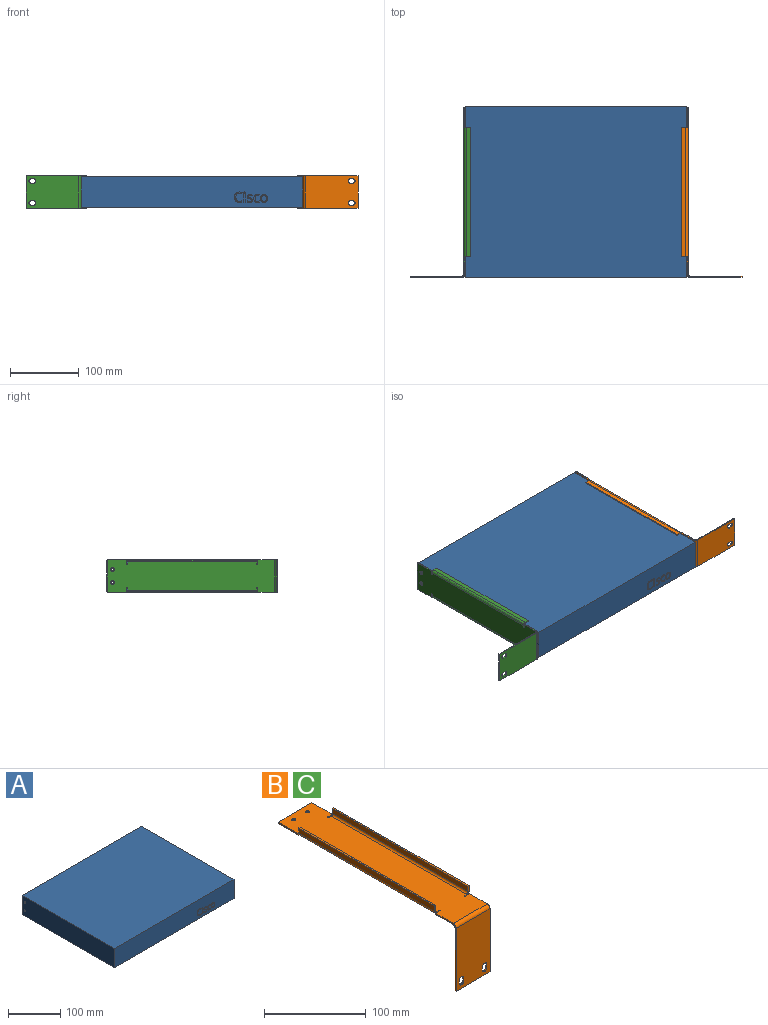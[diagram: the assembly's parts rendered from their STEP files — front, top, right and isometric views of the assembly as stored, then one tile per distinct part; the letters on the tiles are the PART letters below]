
ASSEMBLY  parts=3 mates=4
PART A: 99 faces, bbox 323x248.5x44.5 mm
  f0: plane 323x44.5mm, normal (0,-1,0), area 14138.3mm2, adj f2,f3,f4,f5,f15,f16,f17,f18
  f1: plane 323x44.5mm, normal (0,1,0), area 14373.5mm2, adj f2,f3,f4,f5
  f2: plane 248.5x44.5mm, normal (-1,0,0), area 11033.1mm2, adj f0,f1,f4,f5,f6,f7
  f3: plane 248.5x44.5mm, normal (1,0,0), area 11033.1mm2, adj f0,f1,f4,f5,f6,f7
  f4: plane 323x248.5mm, normal (0,0,1), area 80265.5mm2, adj f0,f1,f2,f3
  f5: plane 323x248.5mm, normal (0,0,-1), area 80265.5mm2, adj f0,f1,f2,f3
  f6: cylinder r=2mm len=323mm, axis (1,0,0), area 4058.9mm2, adj f2,f3
  f7: cylinder r=2mm len=323mm, axis (1,0,0), area 4058.9mm2, adj f2,f3
  f8: extruded ~5x3.23mm, area 17mm2, adj f9,f24,f25,f98
  f9: extruded ~5x3.22mm, area 16.9mm2, adj f8,f10,f25,f98
  f10: extruded ~5x2.48mm, area 14.1mm2, adj f9,f11,f25,f98
  f11: extruded ~5x2.52mm, area 14.3mm2, adj f10,f12,f25,f98
  f12: extruded ~5x3.21mm, area 16.9mm2, adj f11,f13,f25,f98
  f13: extruded ~5x3.24mm, area 17mm2, adj f12,f14,f25,f98
  f14: extruded ~5x2.5mm, area 14.2mm2, adj f13,f24,f25,f98
  f15: extruded ~5x4.23mm, area 22.7mm2, adj f0,f16,f23,f25
  f16: extruded ~5x4.18mm, area 22.5mm2, adj f0,f15,f17,f25
  f17: extruded ~5x3.69mm, area 20.7mm2, adj f0,f16,f18,f25
  f18: extruded ~5x3.76mm, area 20.9mm2, adj f0,f17,f19,f25
  f19: extruded ~5x4.22mm, area 22.7mm2, adj f0,f18,f20,f25
  f20: extruded ~5x3.05mm, area 15.7mm2, adj f0,f19,f21,f25
  f21: extruded ~5x2mm, area 13.6mm2, adj f0,f20,f22,f25
  f22: extruded ~5x2.64mm, area 13.8mm2, adj f0,f21,f23,f25
  f23: extruded ~5x3.77mm, area 21mm2, adj f0,f15,f22,f25
  f24: extruded ~5x2.49mm, area 14.2mm2, adj f8,f14,f25,f98
  f25: plane 11.48x10.17mm, normal (0,-1,0), area 47.1mm2, adj f8,f9,f10,f11,f12,f13,f14,f15
  f26: extruded ~5x3.72mm, area 20.7mm2, adj f0,f27,f40,f41
  f27: extruded ~5x2.8mm, area 14.4mm2, adj f0,f26,f28,f41
  f28: plane 5x1.48mm, normal (-1,0,0), area 7.4mm2, adj f0,f27,f29,f41
  f29: extruded ~5x2.84mm, area 14.6mm2, adj f0,f28,f30,f41
  f30: extruded ~5x2.44mm, area 13.9mm2, adj f0,f29,f31,f41
  f31: extruded ~5x3.13mm, area 16.5mm2, adj f0,f30,f32,f41
  f32: extruded ~5x4.3mm, area 31.2mm2, adj f0,f31,f33,f41
  f33: extruded ~5x1.16mm, area 5.9mm2, adj f0,f32,f34,f41
  f34: extruded ~5x1.21mm, area 6.3mm2, adj f0,f33,f35,f41
  f35: plane 5x1.42mm, normal (-0.94,0,0.34), area 7.6mm2, adj f0,f34,f36,f41
  f36: extruded ~5x1.25mm, area 6.6mm2, adj f0,f35,f37,f41
  f37: extruded ~5x1.6mm, area 8mm2, adj f0,f36,f38,f41
  f38: extruded ~5x3.81mm, area 21.2mm2, adj f0,f37,f39,f41
  f39: extruded ~5x4.29mm, area 23mm2, adj f0,f38,f40,f41
  f40: extruded ~5x4.19mm, area 22.5mm2, adj f0,f26,f39,f41
  f41: plane 11.48x8mm, normal (0,-1,0), area 32.5mm2, adj f26,f27,f28,f29,f30,f31,f32,f33
  f42: extruded ~5x2.38mm, area 13.8mm2, adj f0,f43,f66,f67
  f43: extruded ~5x1.83mm, area 10mm2, adj f0,f42,f44,f67
  f44: extruded ~5x2.66mm, area 15.3mm2, adj f0,f43,f45,f67
  f45: extruded ~5x1.94mm, area 10.5mm2, adj f0,f44,f46,f67
  f46: extruded ~5x0.73mm, area 4.8mm2, adj f0,f45,f47,f67
  f47: extruded ~5x0.76mm, area 4mm2, adj f0,f46,f48,f67
  f48: extruded ~5x1.03mm, area 6.3mm2, adj f0,f47,f49,f67
  f49: extruded ~5x1.8mm, area 9.3mm2, adj f0,f48,f50,f67
  f50: extruded ~5x3.02mm, area 15.6mm2, adj f0,f49,f51,f67
  f51: plane 5x1.36mm, normal (-0.92,0,0.4), area 7.4mm2, adj f0,f50,f52,f67
  f52: extruded ~5x3.5mm, area 18mm2, adj f0,f51,f53,f67
  f53: extruded ~5x3.02mm, area 15.8mm2, adj f0,f52,f54,f67
  f54: extruded ~5x2.14mm, area 12.5mm2, adj f0,f53,f55,f67
  f55: extruded ~5x1.3mm, area 6.8mm2, adj f0,f54,f56,f67
  f56: extruded ~5x0.97mm, area 6.9mm2, adj f0,f55,f57,f67
  f57: extruded ~5x2.2mm, area 12.1mm2, adj f0,f56,f58,f67
  f58: extruded ~5x2.19mm, area 12.3mm2, adj f0,f57,f59,f67
  f59: extruded ~5x1.11mm, area 6.4mm2, adj f0,f58,f60,f67
  f60: extruded ~5x1.28mm, area 7.7mm2, adj f0,f59,f61,f67
  f61: extruded ~5x2.02mm, area 10.4mm2, adj f0,f60,f62,f67
  f62: extruded ~5x1.76mm, area 8.9mm2, adj f0,f61,f63,f67
  f63: extruded ~5x1.71mm, area 9.1mm2, adj f0,f62,f64,f67
  f64: plane 5x1.56mm, normal (1,0,0), area 7.8mm2, adj f0,f63,f65,f67
  f65: extruded ~5x3.43mm, area 17.7mm2, adj f0,f64,f66,f67
  f66: extruded ~5x3.23mm, area 17mm2, adj f0,f42,f65,f67
  f67: plane 11.48x7.85mm, normal (0,-1,0), area 37.6mm2, adj f42,f43,f44,f45,f46,f47,f48,f49
  f68: extruded ~5x0.84mm, area 4.6mm2, adj f0,f69,f75,f76
  f69: extruded ~5x0.84mm, area 4.6mm2, adj f0,f68,f70,f76
  f70: extruded ~5x0.71mm, area 3.9mm2, adj f0,f69,f71,f76
  f71: extruded ~5x0.7mm, area 3.8mm2, adj f0,f70,f72,f76
  f72: extruded ~5x0.84mm, area 4.6mm2, adj f0,f71,f73,f76
  f73: extruded ~5x0.84mm, area 4.6mm2, adj f0,f72,f74,f76
  f74: extruded ~5x0.7mm, area 3.8mm2, adj f0,f73,f75,f76
  f75: extruded ~5x0.71mm, area 3.9mm2, adj f0,f68,f74,f76
  f76: plane 2.23x1.98mm, normal (0,-1,0), area 3.6mm2, adj f68,f69,f70,f71,f72,f73,f74,f75
  f77: plane 5x1.68mm, normal (0,0,1), area 8.4mm2, adj f0,f78,f80,f81
  f78: plane 11.07x5mm, normal (-1,0,0), area 55.4mm2, adj f0,f77,f79,f81
  f79: plane 5x1.68mm, normal (0,0,-1), area 8.4mm2, adj f0,f78,f80,f81
  f80: plane 11.07x5mm, normal (1,0,0), area 55.4mm2, adj f0,f77,f79,f81
  f81: plane 11.07x1.68mm, normal (0,-1,0), area 18.6mm2, adj f77,f78,f79,f80
  f82: extruded ~5x3.84mm, area 21.6mm2, adj f0,f83,f96,f97
  f83: extruded ~5x3.36mm, area 17.4mm2, adj f0,f82,f84,f97
  f84: plane 5x1.47mm, normal (-0.9,0,0.44), area 8.2mm2, adj f0,f83,f85,f97
  f85: extruded ~5x4.06mm, area 20.9mm2, adj f0,f84,f86,f97
  f86: extruded ~5x3.79mm, area 19.8mm2, adj f0,f85,f87,f97
  f87: extruded ~5x2.65mm, area 18.4mm2, adj f0,f86,f88,f97
  f88: extruded ~5x4mm, area 20.6mm2, adj f0,f87,f89,f97
  f89: extruded ~5.63x5mm, area 30.2mm2, adj f0,f88,f90,f97
  f90: extruded ~5.04x5mm, area 27.9mm2, adj f0,f89,f91,f97
  f91: extruded ~5x3.79mm, area 19.3mm2, adj f0,f90,f92,f97
  f92: plane 5x1.5mm, normal (-1,0,0), area 7.5mm2, adj f0,f91,f93,f97
  f93: extruded ~5x3.53mm, area 17.9mm2, adj f0,f92,f94,f97
  f94: extruded ~5x3.87mm, area 21.6mm2, adj f0,f93,f95,f97
  f95: extruded ~5x4.48mm, area 23.9mm2, adj f0,f94,f96,f97
  f96: extruded ~5x4.44mm, area 23.8mm2, adj f0,f82,f95,f97
  f97: plane 15.18x11.17mm, normal (0,-1,0), area 47.7mm2, adj f82,f83,f84,f85,f86,f87,f88,f89
  f98: plane 8.65x6.7mm, normal (0,-1,0), area 48.1mm2, adj f8,f9,f10,f11,f12,f13,f14,f24
PART B: 58 faces, bbox 48.7x248x88.4 mm
  f0: plane 3.5x1.6mm, normal (-1,0,0), area 5.6mm2, adj f1,f10,f11,f12
  f1: cylinder r=3.25mm len=6.5mm, axis (0,1,0), area 16.3mm2, adj f0,f2,f11,f12
  f2: plane 3.5x1.6mm, normal (1,0,0), area 5.6mm2, adj f1,f10,f11,f12
  f3: plane 3.5x1.6mm, normal (-1,0,0), area 5.6mm2, adj f4,f9,f11,f12
  f4: cylinder r=3.25mm len=6.5mm, axis (0,1,0), area 16.3mm2, adj f3,f5,f11,f12
  f5: plane 3.5x1.6mm, normal (1,0,0), area 5.6mm2, adj f4,f9,f11,f12
  f6: plane 76.1x1.6mm, normal (-1,0,0), area 121.8mm2, adj f8,f11,f12,f53
  f7: plane 76.1x1.6mm, normal (1,0,0), area 121.8mm2, adj f8,f11,f12,f52
  f8: plane 47.1x1.6mm, normal (0,0,-1), area 75.4mm2, adj f6,f7,f11,f12
  f9: cylinder r=3.25mm len=6.5mm, axis (0,1,0), area 16.3mm2, adj f3,f5,f11,f12
  f10: cylinder r=3.25mm len=6.5mm, axis (0,1,0), area 16.3mm2, adj f0,f2,f11,f12
  f11: plane 76.1x47.1mm, normal (0,1,0), area 3472.4mm2, adj f0,f1,f2,f3,f4,f5,f6,f7
  f12: plane 76.1x47.1mm, normal (0,-1,0), area 3472.4mm2, adj f0,f1,f2,f3,f4,f5,f6,f7
  f13: plane 24.4x1.6mm, normal (-1,0,0), area 39mm2, adj f15,f16,f24,f53
  f14: plane 28.3x1.6mm, normal (1,0,0), area 45.3mm2, adj f15,f16,f18,f30
  f15: plane 244.1x47.1mm, normal (0,0,-1), area 10231.7mm2, adj f13,f14,f17,f18,f19,f22,f23,f24
  f16: plane 244.1x47.1mm, normal (0,0,1), area 10263.1mm2, adj f13,f14,f17,f18,f19,f20,f21,f22
  f17: plane 28.3x1.6mm, normal (-1,0,0), area 45.3mm2, adj f15,f16,f18,f27
  f18: plane 47.1x1.6mm, normal (0,1,0), area 75.4mm2, adj f14,f15,f16,f17
  f19: plane 24.4x1.6mm, normal (1,0,0), area 39mm2, adj f15,f16,f33,f52
  f20: cylinder r=2mm len=4mm, axis (0,0,-1), area 7.5mm2, adj f16,f56
  f21: cylinder r=2mm len=4mm, axis (0,0,-1), area 7.5mm2, adj f16,f57
  f22: cylinder r=0.85mm len=1.7mm, axis (0,0,1), area 4.3mm2, adj f15,f16,f23,f24
  f23: plane 2.6x1.6mm, normal (0,-1,0), area 4.2mm2, adj f15,f16,f22,f40
  f24: plane 5.7x1.6mm, normal (0,1,0), area 9.1mm2, adj f13,f15,f16,f22
  f25: cylinder r=0.85mm len=1.7mm, axis (0,0,1), area 4.3mm2, adj f15,f16,f26,f27
  f26: plane 2.6x1.6mm, normal (0,1,0), area 4.2mm2, adj f15,f16,f25,f39
  f27: plane 5.7x1.6mm, normal (0,-1,0), area 9.1mm2, adj f15,f16,f17,f25
  f28: cylinder r=0.85mm len=1.7mm, axis (0,0,1), area 4.3mm2, adj f15,f16,f29,f30
  f29: plane 2.6x1.6mm, normal (0,1,0), area 4.2mm2, adj f15,f16,f28,f49
  f30: plane 5.7x1.6mm, normal (0,-1,0), area 9.1mm2, adj f14,f15,f16,f28
  f31: cylinder r=0.85mm len=1.7mm, axis (0,0,1), area 4.3mm2, adj f15,f16,f32,f33
  f32: plane 2.6x1.6mm, normal (0,-1,0), area 4.2mm2, adj f15,f16,f31,f48
  f33: plane 5.7x1.6mm, normal (0,1,0), area 9.1mm2, adj f15,f16,f19,f31
  f34: plane 6.1x1.6mm, normal (0,1,0), area 9.8mm2, adj f36,f37,f38,f39
  f35: plane 6.1x1.6mm, normal (0,-1,0), area 9.8mm2, adj f36,f37,f38,f40
  f36: plane 188x1.6mm, normal (0,0,1), area 300.8mm2, adj f34,f35,f37,f38
  f37: plane 188x6.1mm, normal (-1,0,0), area 1146.8mm2, adj f34,f35,f36,f41
  f38: plane 188x6.1mm, normal (1,0,0), area 1146.8mm2, adj f34,f35,f36,f42
  f39: plane 3.9x3.9mm, normal (0,1,0), area 7.8mm2, adj f26,f34,f41,f42
  f40: plane 3.9x3.9mm, normal (0,-1,0), area 7.8mm2, adj f23,f35,f41,f42
  f41: cylinder r=3.9mm len=188mm, axis (0,1,0), area 1151.7mm2, adj f15,f37,f39,f40
  f42: cylinder r=2.3mm len=188mm, axis (0,1,0), area 679.2mm2, adj f16,f38,f39,f40
  f43: plane 6.1x1.6mm, normal (0,-1,0), area 9.8mm2, adj f45,f46,f47,f48
  f44: plane 6.1x1.6mm, normal (0,1,0), area 9.8mm2, adj f45,f46,f47,f49
  f45: plane 188x1.6mm, normal (0,0,1), area 300.8mm2, adj f43,f44,f46,f47
  f46: plane 188x6.1mm, normal (1,0,0), area 1146.8mm2, adj f43,f44,f45,f50
  f47: plane 188x6.1mm, normal (-1,0,0), area 1146.8mm2, adj f43,f44,f45,f51
  f48: plane 3.9x3.9mm, normal (0,-1,0), area 7.8mm2, adj f32,f43,f50,f51
  f49: plane 3.9x3.9mm, normal (0,1,0), area 7.8mm2, adj f29,f44,f50,f51
  f50: cylinder r=3.9mm len=188mm, axis (0,-1,0), area 1151.7mm2, adj f15,f46,f48,f49
  f51: cylinder r=2.3mm len=188mm, axis (0,-1,0), area 679.2mm2, adj f16,f47,f48,f49
  f52: plane 3.9x3.9mm, normal (1,0,0), area 7.8mm2, adj f7,f19,f54,f55
  f53: plane 3.9x3.9mm, normal (-1,0,0), area 7.8mm2, adj f6,f13,f54,f55
  f54: cylinder r=3.9mm len=47.1mm, axis (1,0,0), area 288.5mm2, adj f12,f16,f52,f53
  f55: cylinder r=2.3mm len=47.1mm, axis (1,0,0), area 170.2mm2, adj f11,f15,f52,f53
  f56: cone r=3mm half-angle=45deg, axis (0,0,-1), area 22.2mm2, adj f15,f20
  f57: cone r=3mm half-angle=45deg, axis (0,0,-1), area 22.2mm2, adj f15,f21
PART C: same geometry as B
PLACE A rot(axis=(-0.02,1,0.04),0deg) t=(162.29,141.25,-27.34)mm
PLACE B rot(axis=(0,-1,0),90deg) t=(324.19,17,-27.27)mm
PLACE C rot(axis=(0,1,0),90deg) t=(0.39,17,-27.27)mm
MATE pin_slot A.f7 <-> B.f21  axis (1,0,0) through (323.79,257.5,-17.77)mm
MATE parallel B.f16 <-> A.f3  axis (-1,0,0) through (324.19,142.9,-27.27)mm
MATE parallel C.f16 <-> A.f2  axis (1,0,0) through (0.39,142.9,-27.27)mm
MATE pin_slot A.f7 <-> C.f20  axis (-1,0,0) through (0.79,257.5,-17.77)mm
